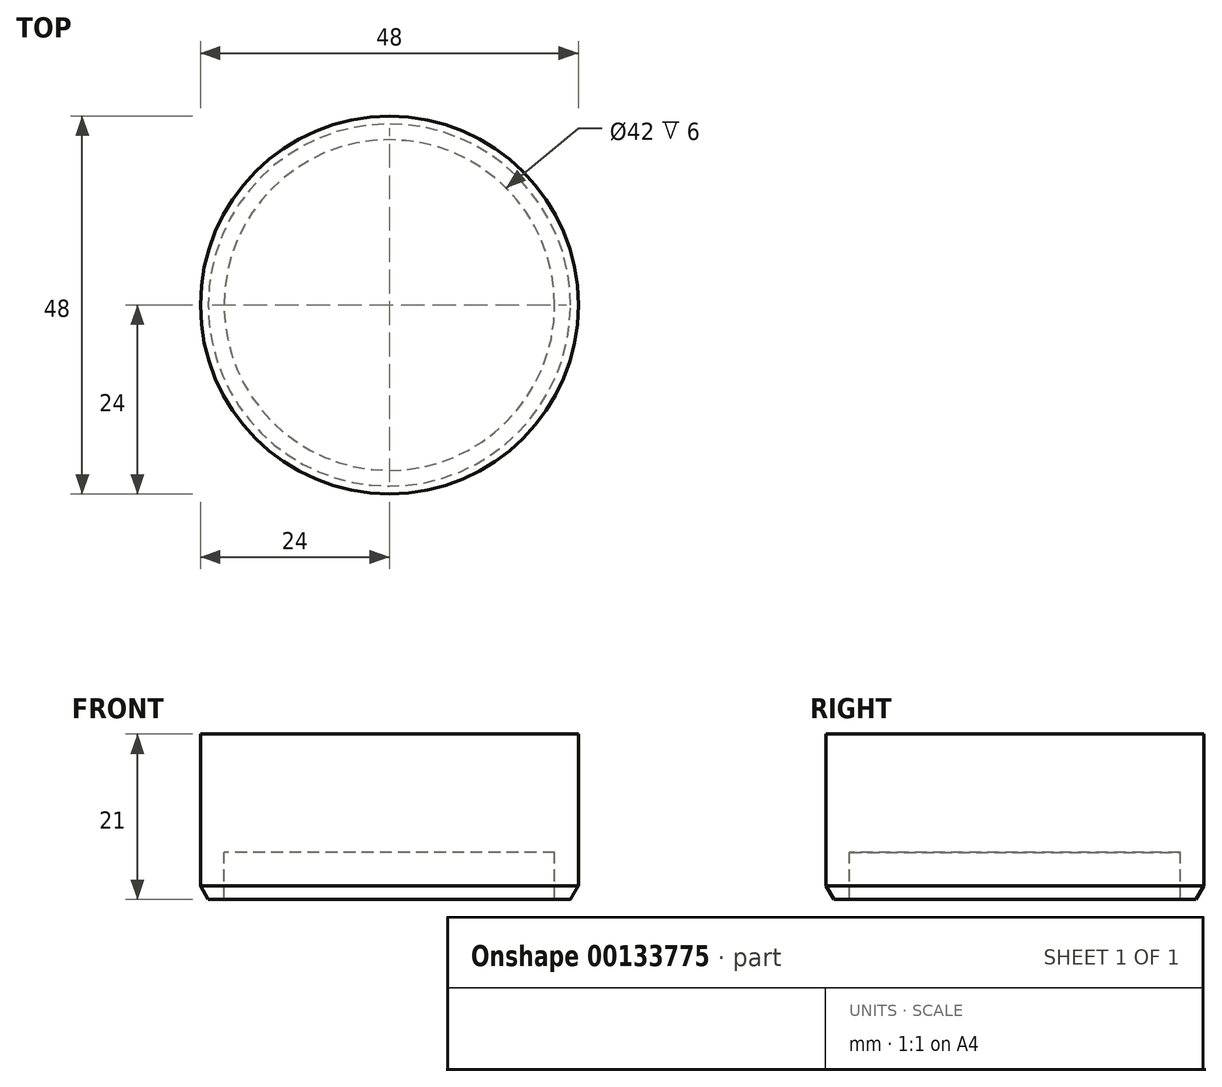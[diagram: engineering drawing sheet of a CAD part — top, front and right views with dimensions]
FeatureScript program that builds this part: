
annotation { "Feature Type Name" : "Feature", "Feature Type Description" : "" }
export const myFeature = defineFeature(function(context is Context, id is Id, definition is map)
    precondition{}
    {
        {
            var Q0;
            Q0=qCreatedBy(makeId("Right.planeOp"),FACE);
            var sketch = newSketch(context, id + "F0", { "sketchPlane" : qUnion([Q0])});
            skLineSegment(sketch, "E0", {"start": v(21, 0) * mm, "end": v(23, 0) * mm});
            skLineSegment(sketch, "E1", {"start": v(23, 0) * mm, "end": v(24, 1.73) * mm});
            skLineSegment(sketch, "E2", {"start": v(24, 1.73) * mm, "end": v(24, 21) * mm});
            skLineSegment(sketch, "E3", {"start": v(24, 21) * mm, "end": v(0, 21) * mm});
            skLineSegment(sketch, "E4", {"start": v(0, 21) * mm, "end": v(0, 6) * mm});
            skLineSegment(sketch, "E5", {"start": v(0, 6) * mm, "end": v(21, 6) * mm});
            skLineSegment(sketch, "E6", {"start": v(21, 6) * mm, "end": v(21, 0) * mm});
            skSolve(sketch);
        }
        {
            var Q0;
            Q0 = qSketchRegion(id + "F0", true);
            var Q1;
            Q1=sQuery(id+"F0.wireOp",EDGE,"E4");
            revolve(context, id + "F1", {"entities" : qUnion([Q0]), "axis" : qUnion([Q1]), "revolveType" : RevolveType.FULL});
        }
    });
